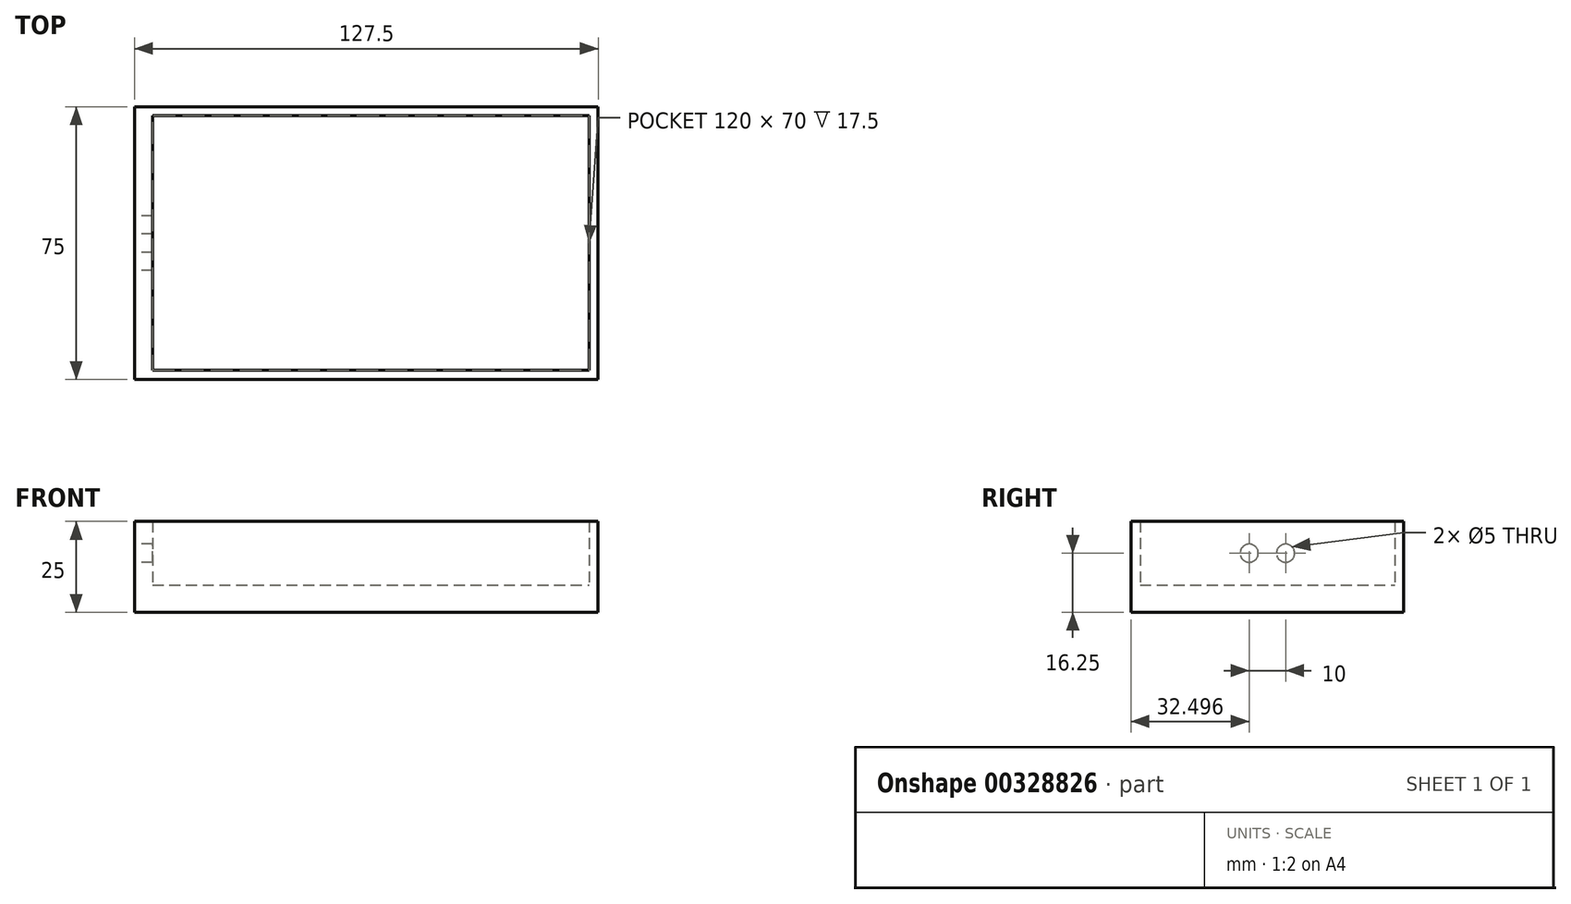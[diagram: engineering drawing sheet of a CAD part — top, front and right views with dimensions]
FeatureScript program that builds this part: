
annotation { "Feature Type Name" : "Feature", "Feature Type Description" : "" }
export const myFeature = defineFeature(function(context is Context, id is Id, definition is map)
    precondition{}
    {
        {
            var Q0;
            Q0=qCreatedBy(makeId("Top.planeOp"),FACE);
            var sketch = newSketch(context, id + "F0", { "sketchPlane" : qUnion([Q0])});
            skLineSegment(sketch, "E0.bottom", {"start": v(-166.21, -67.61) * mm, "end": v(-46.21, -67.61) * mm});
            skLineSegment(sketch, "E0.top", {"start": v(-166.21, -137.61) * mm, "end": v(-46.21, -137.61) * mm});
            skLineSegment(sketch, "E0.left", {"start": v(-166.21, -67.61) * mm, "end": v(-166.21, -137.61) * mm});
            skLineSegment(sketch, "E0.right", {"start": v(-46.21, -67.61) * mm, "end": v(-46.21, -137.61) * mm});
            skLineSegment(sketch, "E1.bottom", {"start": v(-171.21, -65.11) * mm, "end": v(-43.71, -65.11) * mm});
            skLineSegment(sketch, "E1.top", {"start": v(-171.21, -140.11) * mm, "end": v(-43.71, -140.11) * mm});
            skLineSegment(sketch, "E1.left", {"start": v(-171.21, -65.11) * mm, "end": v(-171.21, -140.11) * mm});
            skLineSegment(sketch, "E1.right", {"start": v(-43.71, -65.11) * mm, "end": v(-43.71, -140.11) * mm});
            skSolve(sketch);
        }
        {
            var Q0;
            Q0=makeQuery(id+"F0.imprint","IMPRINT",FACE,{"disambiguationData":[TD([[makeQuery(id+"F0.imprint","IMPRINT",EDGE,{"derivedFrom":sQuery(id+"F0.wireOp",EDGE,"E0.bottom")}),1.0]])]});
            extrude(context, id + "F1", {"entities" : qUnion([Q0]), "depth" : 25 * mm});
        }
        {
            var Q0;
            Q0=makeQuery(id+"F1.opExtrude","SWEPT_FACE",FACE,{"disambiguationData":[OSD([sQuery(id+"F0.wireOp",EDGE,"E0.bottom")])]});
            var sketch = newSketch(context, id + "F2", { "sketchPlane" : qUnion([Q0])});
            skLineSegment(sketch, "E2.bottom", {"start": v(-166.21, 0) * mm, "end": v(13.79, 0) * mm});
            skLineSegment(sketch, "E2.top", {"start": v(-166.21, 7.5) * mm, "end": v(13.79, 7.5) * mm});
            skLineSegment(sketch, "E2.left", {"start": v(-166.21, 0) * mm, "end": v(-166.21, 7.5) * mm});
            skLineSegment(sketch, "E2.right", {"start": v(13.79, 0) * mm, "end": v(13.79, 7.5) * mm});
            skSolve(sketch);
        }
        {
            var Q0;
            {var subQ0=sQuery(id+"F2.wireOp",EDGE,"E2.left");Q0=makeQuery(id+"F2.imprint","IMPRINT",FACE,{"disambiguationData":[TD([[makeQuery(id+"F2.imprint","IMPRINT",EDGE,{"derivedFrom":subQ0}),1.0]])]});}
            extrude(context, id + "F3", {"entities" : qUnion([Q0]), "operationType" : NewBodyOperationType.ADD, "depth" : 70 * mm});
        }
        {
            var Q0;
            Q0=makeQuery(id+"F1.opExtrude","SWEPT_FACE",FACE,{"disambiguationData":[OSD([sQuery(id+"F0.wireOp",EDGE,"E1.left")])]});
            var sketch = newSketch(context, id + "F4", { "sketchPlane" : qUnion([Q0])});
            skLineSegment(sketch, "E3.0.0", {"start": v(65.11, 0) * mm, "end": v(140.11, 0) * mm});
            skLineSegment(sketch, "E3.0.1", {"start": v(140.11, 0) * mm, "end": v(140.11, 25) * mm});
            skLineSegment(sketch, "E3.0.2", {"start": v(140.11, 25) * mm, "end": v(65.11, 25) * mm});
            skLineSegment(sketch, "E3.0.3", {"start": v(65.11, 25) * mm, "end": v(65.11, 0) * mm});
            skLineSegment(sketch, "E4.0.0", {"start": v(67.61, 7.5) * mm, "end": v(137.61, 7.5) * mm});
            skLineSegment(sketch, "E4.0.1", {"start": v(137.61, 7.5) * mm, "end": v(137.61, 25) * mm});
            skLineSegment(sketch, "E4.0.2", {"start": v(137.61, 25) * mm, "end": v(67.61, 25) * mm});
            skLineSegment(sketch, "E4.0.3", {"start": v(67.61, 25) * mm, "end": v(67.61, 7.5) * mm});
            skCircle(sketch, "E5", {"center": v(97.61, 16.25) * mm, "radius": 2.5 * mm});
            skPoint(sketch, "E5.centerSnap0", {"position": v(67.61, 16.25) * mm});
            skLineSegment(sketch, "E6", {"start": v(102.61, 7.5) * mm, "end": v(102.61, 25) * mm});
            skCircle(sketch, "E7", {"center": v(107.61, 16.25) * mm, "radius": 2.5 * mm});
            skSolve(sketch);
        }
        {
            var Q0;
            Q0=makeQuery(id+"F4.imprint","IMPRINT",FACE,{"disambiguationData":[TD([[makeQuery(id+"F4.imprint","IMPRINT",EDGE,{"derivedFrom":sQuery(id+"F4.wireOp",EDGE,"E5")}),1.0]])]});
            var Q1;
            Q1=makeQuery(id+"F4.imprint","IMPRINT",FACE,{"disambiguationData":[TD([[makeQuery(id+"F4.imprint","IMPRINT",EDGE,{"derivedFrom":sQuery(id+"F4.wireOp",EDGE,"E7")}),1.0]])]});
            extrude(context, id + "F5", {"entities" : qUnion([Q0, Q1]), "operationType" : NewBodyOperationType.REMOVE, "oppositeDirection" : true, "depth" : 25 * mm});
        }
    });
